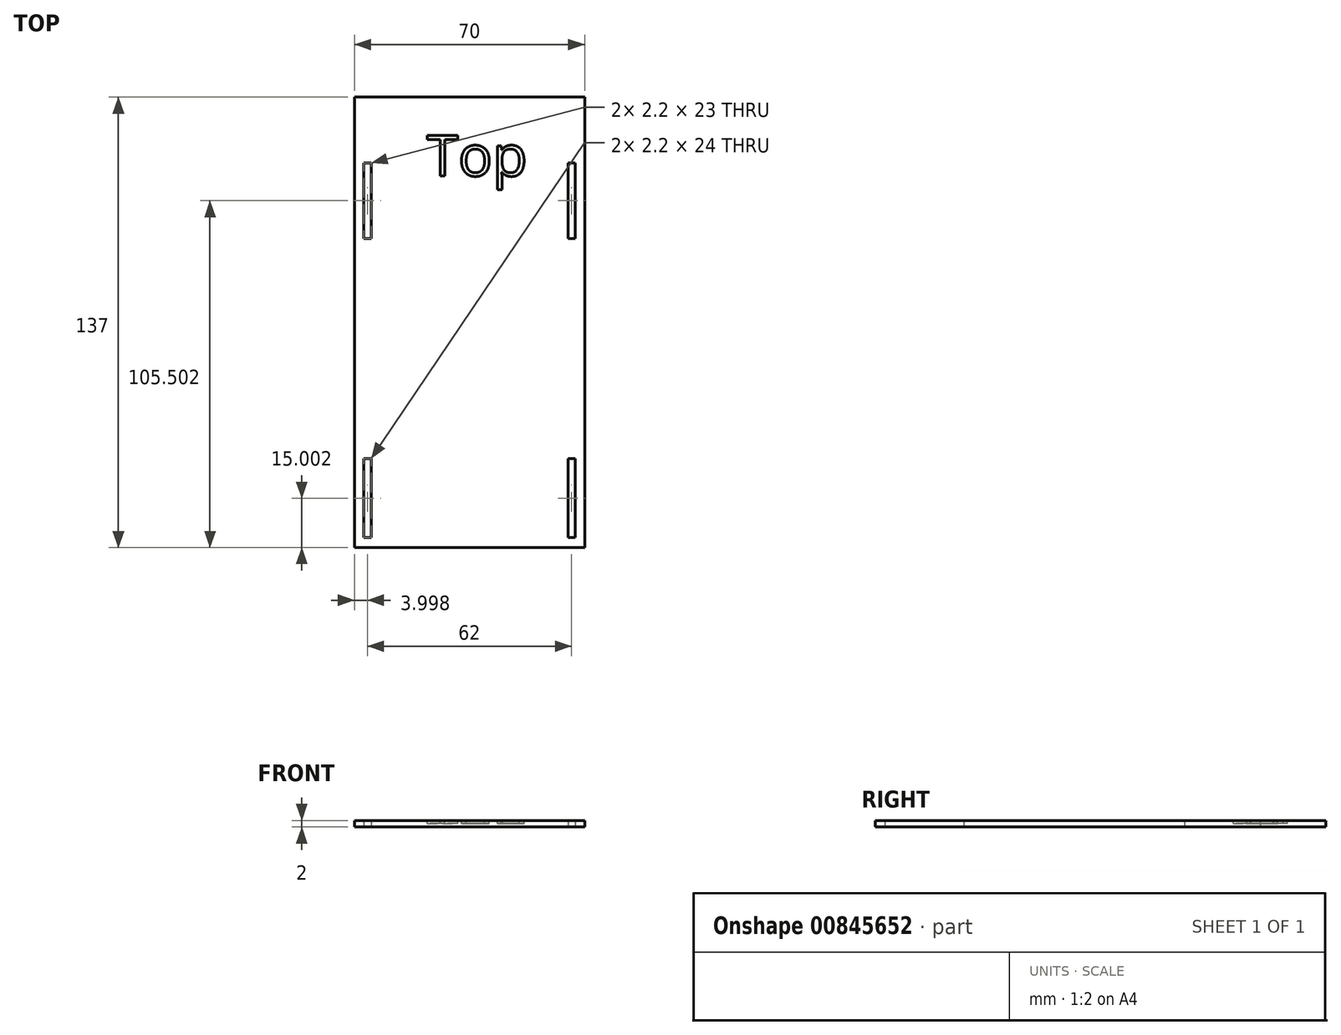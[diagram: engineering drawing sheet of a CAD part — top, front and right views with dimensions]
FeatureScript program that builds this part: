
annotation { "Feature Type Name" : "Feature", "Feature Type Description" : "" }
export const myFeature = defineFeature(function(context is Context, id is Id, definition is map)
    precondition{}
    {
        {
            var Q0;
            Q0=qCreatedBy(makeId("Top.planeOp"),FACE);
            var sketch = newSketch(context, id + "F0", { "sketchPlane" : qUnion([Q0])});
            skLineSegment(sketch, "E0.bottom", {"start": v(-36.45, 82.6) * mm, "end": v(33.55, 82.6) * mm});
            skLineSegment(sketch, "E0.top", {"start": v(-36.45, -54.4) * mm, "end": v(33.55, -54.4) * mm});
            skLineSegment(sketch, "E0.left", {"start": v(-36.45, 82.6) * mm, "end": v(-36.45, -54.4) * mm});
            skLineSegment(sketch, "E0.right", {"start": v(33.55, 82.6) * mm, "end": v(33.55, -54.4) * mm});
            skSolve(sketch);
        }
        {
            var Q0;
            Q0 = qSketchRegion(id + "F0", true);
            extrude(context, id + "F1", {"entities" : qUnion([Q0]), "depth" : 2 * mm, "offsetDistance" : 25 * mm});
        }
        {
            var Q0;
            Q0=qCreatedBy(makeId("Top.planeOp"),FACE);
            var sketch = newSketch(context, id + "F2", { "sketchPlane" : qUnion([Q0])});
            skLineSegment(sketch, "E1.0", {"start": v(-48.65, 62.6) * mm, "end": v(70.42, 62.6) * mm, "construction": true});
            skLineSegment(sketch, "E1.1", {"start": v(28.45, 90.45) * mm, "end": v(28.45, -79.59) * mm, "construction": true});
            skLineSegment(sketch, "E1.2", {"start": v(30.65, 93.05) * mm, "end": v(30.65, -81.96) * mm, "construction": true});
            skLineSegment(sketch, "E1.3", {"start": v(-31.35, 94.76) * mm, "end": v(-31.35, -66.43) * mm, "construction": true});
            skLineSegment(sketch, "E1.4", {"start": v(-33.55, 92.02) * mm, "end": v(-33.55, -67.6) * mm, "construction": true});
            skLineSegment(sketch, "E1.5", {"start": v(-59.94, 39.6) * mm, "end": v(64, 39.6) * mm, "construction": true});
            skLineSegment(sketch, "E2", {"start": v(-51.1, -27.4) * mm, "end": v(65.4, -27.4) * mm, "construction": true});
            skLineSegment(sketch, "E3", {"start": v(58.34, -51.4) * mm, "end": v(-53.54, -51.4) * mm, "construction": true});
            skLineSegment(sketch, "E4.bottom", {"start": v(-33.55, 62.6) * mm, "end": v(-31.35, 62.6) * mm});
            skLineSegment(sketch, "E4.top", {"start": v(-33.55, 39.6) * mm, "end": v(-31.35, 39.6) * mm});
            skLineSegment(sketch, "E4.left", {"start": v(-33.55, 62.6) * mm, "end": v(-33.55, 39.6) * mm});
            skLineSegment(sketch, "E4.right", {"start": v(-31.35, 62.6) * mm, "end": v(-31.35, 39.6) * mm});
            skLineSegment(sketch, "E5.bottom", {"start": v(28.45, 62.6) * mm, "end": v(30.65, 62.6) * mm});
            skLineSegment(sketch, "E5.top", {"start": v(28.45, 39.6) * mm, "end": v(30.65, 39.6) * mm});
            skLineSegment(sketch, "E5.left", {"start": v(28.45, 62.6) * mm, "end": v(28.45, 39.6) * mm});
            skLineSegment(sketch, "E5.right", {"start": v(30.65, 62.6) * mm, "end": v(30.65, 39.6) * mm});
            skLineSegment(sketch, "E6.bottom", {"start": v(-33.55, -27.4) * mm, "end": v(-31.35, -27.4) * mm});
            skLineSegment(sketch, "E6.top", {"start": v(-33.55, -51.4) * mm, "end": v(-31.35, -51.4) * mm});
            skLineSegment(sketch, "E6.left", {"start": v(-33.55, -27.4) * mm, "end": v(-33.55, -51.4) * mm});
            skLineSegment(sketch, "E6.right", {"start": v(-31.35, -27.4) * mm, "end": v(-31.35, -51.4) * mm});
            skLineSegment(sketch, "E7.bottom", {"start": v(28.45, -27.4) * mm, "end": v(30.65, -27.4) * mm});
            skLineSegment(sketch, "E7.top", {"start": v(28.45, -51.4) * mm, "end": v(30.65, -51.4) * mm});
            skLineSegment(sketch, "E7.left", {"start": v(28.45, -27.4) * mm, "end": v(28.45, -51.4) * mm});
            skLineSegment(sketch, "E7.right", {"start": v(30.65, -27.4) * mm, "end": v(30.65, -51.4) * mm});
            skSolve(sketch);
        }
        {
            var Q0;
            Q0 = qSketchRegion(id + "F2", true);
            extrude(context, id + "F3", {"entities" : qUnion([Q0]), "operationType" : NewBodyOperationType.REMOVE, "depth" : 25 * mm, "offsetDistance" : 25 * mm});
        }
        {
            var Q0;
            Q0=makeQuery(id+"F1.opExtrude","CAP_FACE",FACE,{"disambiguationData":[OSD([sQuery(id+"F0.wireOp",EDGE,"E0.bottom"),sQuery(id+"F0.wireOp",EDGE,"E0.top"),sQuery(id+"F0.wireOp",EDGE,"E0.left"),sQuery(id+"F0.wireOp",EDGE,"E0.right")])],"isStart":false});
            var sketch = newSketch(context, id + "F4", { "sketchPlane" : qUnion([Q0])});
            skText(sketch, "E8", { "text": "Top", "fontName": "OpenSans-Regular.ttf"});
            const initialGuessF4  = {"E8": [-0.0144, 0.05861, 1, 0, 0.0124]};
            skSetInitialGuess(sketch, initialGuessF4);
            skSolve(sketch);
        }
        {
            var Q0;
            Q0 = qSketchRegion(id + "F4", true);
            extrude(context, id + "F5", {"entities" : qUnion([Q0]), "operationType" : NewBodyOperationType.REMOVE, "oppositeDirection" : true, "depth" : 1 * mm, "offsetDistance" : 25 * mm});
        }
    });
